# Revit family: Скамейка стальная «София» без подлокотников Арт 12130
name_source: partatom
category: Антураж
revit_build: Autodesk Revit 2018 (Build: 20180423_1000(x64)
units: mm (PartAtom-declared; Revit-internal decimal feet)

## family parameters
Всегда вертикально = Да
Источник визуального образа = Геометрия семейства
На основе рабочей плоскости = Нет
Общий = Нет
При загрузке вырезать с полостями = Нет
Точка расчета площади = Нет

## types (5) — shared parameters
URL = https://hobbyka.ru
Артикул товара = Арт. 12130
Высота = 849 мм
Группа модели = Садовые скамейки
Изготовитель = ООО «Хоббика»
Материал изделия = Сталь, дерево
Цвет лавки = Дерево
Цвет опоры = Сталь

## per-type parameters (varying)
| type | Версия 1,5 м | Версия 1,8 м | Версия 2,0 м (3 опоры) | Версия 3,0 м (3 опоры) | Двухсторонняя (1,5 м) | Длина | Изображение типоразмера | Односторонняя | Описание | Средняя опора | Ширина |
| Двухстороння (1,5 м) | Нет | Нет | Нет | Нет | Да | 1500 мм | Скамейка стальная «София» без подлокотников Арт 12130 Двухсторонняя.jpg | Нет | Скамейка стальная «София» без подлокотников. Двухстороння (1,5 м) | Нет | 894 мм |
| Версия 1,5 м | Да | Нет | Нет | Нет | Нет | 1500 мм | Скамейка стальная «София» без подлокотников Арт 12130.jpg | Да | Скамейка стальная «София» без подлокотников. Версия 1,5 м | Нет | 579 мм |
| Версия 1,8 м | Нет | Да | Нет | Нет | Нет | 1800 мм | Скамейка стальная «София» без подлокотников Арт 12130.jpg | Да | Скамейка стальная «София» без подлокотников. Версия 1,8 м | Нет | 579 мм |
| Версия 2,0 м (3 опоры) | Нет | Нет | Да | Нет | Нет | 2000 мм | Скамейка стальная «София» без подлокотников Арт 12130.jpg | Да | Скамейка стальная «София» без подлокотников. Версия 2,0 м (3 опоры) | Да | 579 мм |
| Версия 3,0 м (3 опоры) | Нет | Нет | Нет | Да | Нет | 3000 мм | Скамейка стальная «София» без подлокотников Арт 12130.jpg | Да | Скамейка стальная «София» без подлокотников. Версия 3,0 м (3 опоры) | Да | 579 мм |
